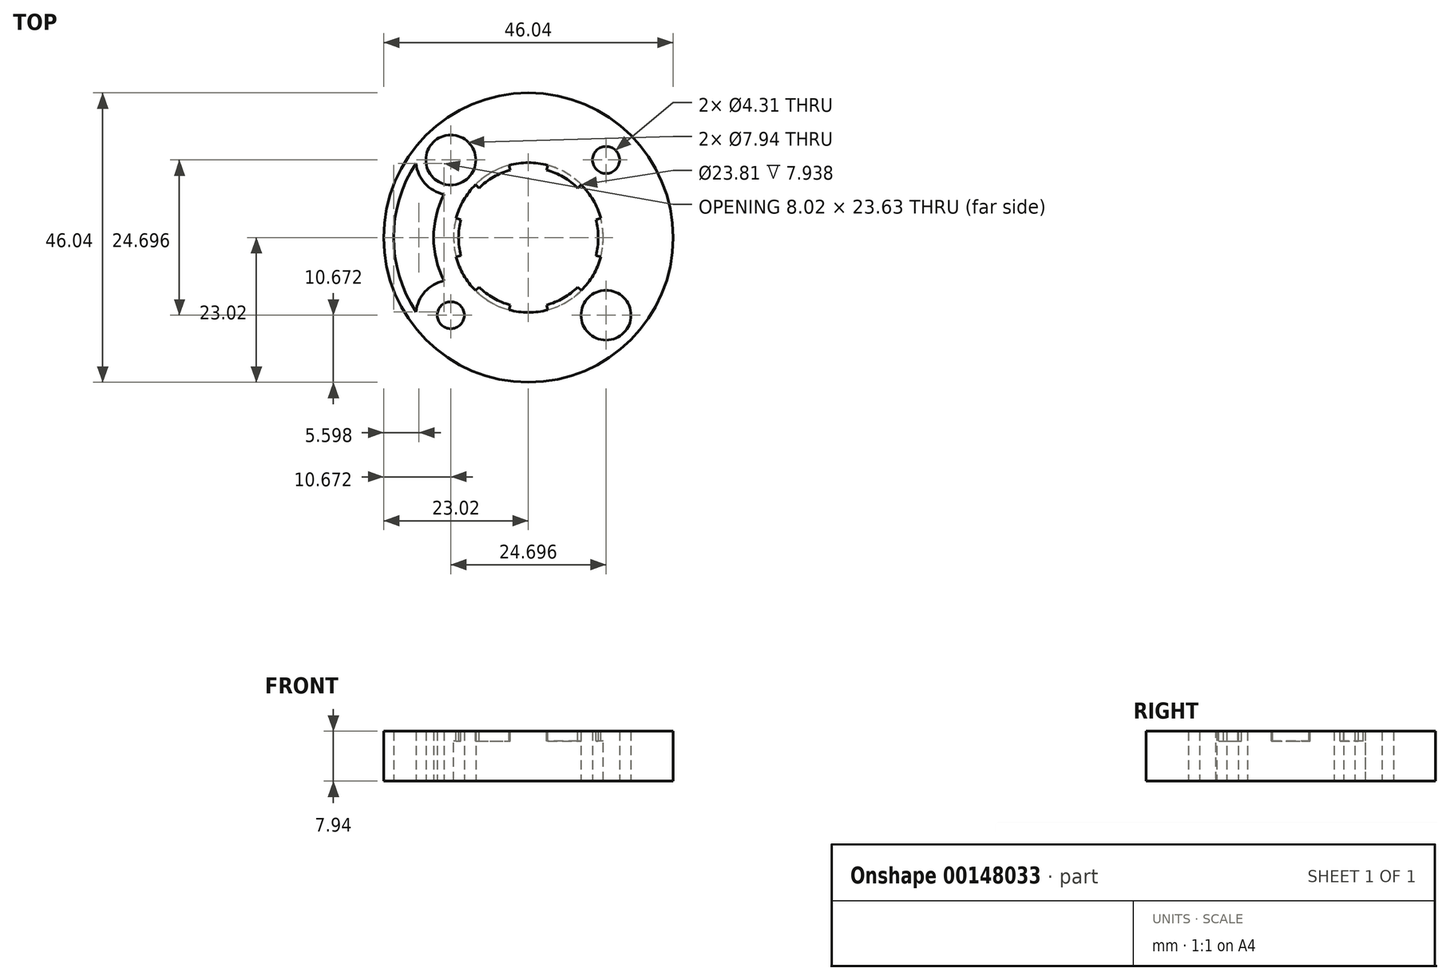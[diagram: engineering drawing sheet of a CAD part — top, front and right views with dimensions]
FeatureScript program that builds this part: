
annotation { "Feature Type Name" : "Feature", "Feature Type Description" : "" }
export const myFeature = defineFeature(function(context is Context, id is Id, definition is map)
    precondition{}
    {
        {
            var Q0;
            Q0=qCreatedBy(makeId("Top.planeOp"),FACE);
            var sketch = newSketch(context, id + "F0", { "sketchPlane" : qUnion([Q0])});
            skCircle(sketch, "E0", {"center": v(0, 0) * mm, "radius": 23.02 * mm});
            skCircle(sketch, "E1", {"center": v(0, 0) * mm, "radius": 11.9 * mm, "construction": true});
            skLineSegment(sketch, "E2.bottom", {"start": v(-12.35, 12.35) * mm, "end": v(12.35, 12.35) * mm, "construction": true});
            skLineSegment(sketch, "E2.top", {"start": v(-12.35, -12.35) * mm, "end": v(12.35, -12.35) * mm, "construction": true});
            skLineSegment(sketch, "E2.left", {"start": v(-12.35, 12.35) * mm, "end": v(-12.35, -12.35) * mm, "construction": true});
            skLineSegment(sketch, "E2.right", {"start": v(12.35, 12.35) * mm, "end": v(12.35, -12.35) * mm, "construction": true});
            skCircle(sketch, "E3", {"center": v(-12.35, 12.35) * mm, "radius": 5.56 * mm, "construction": true});
            skCircle(sketch, "E4", {"center": v(12.35, 12.35) * mm, "radius": 2.15 * mm});
            skCircle(sketch, "E5", {"center": v(-12.35, 12.35) * mm, "radius": 3.97 * mm});
            skCircle(sketch, "E6", {"center": v(-12.35, -12.35) * mm, "radius": 2.15 * mm});
            skCircle(sketch, "E7", {"center": v(12.35, -12.35) * mm, "radius": 3.97 * mm});
            skCircle(sketch, "E8", {"center": v(0, 0) * mm, "radius": 11.11 * mm});
            skSolve(sketch);
        }
        {
            var Q0;
            Q0=qSketchRegion(id+"F0",true);
            extrude(context, id + "F1", {"entities" : qUnion([Q0]), "depth" : 7.94 * mm});
        }
        {
            var Q0;
            Q0=makeQuery(id+"F1.opExtrude","CAP_FACE",FACE,{"disambiguationData":[OSD([sQuery(id+"F0.wireOp",EDGE,"E0"),sQuery(id+"F0.wireOp",EDGE,"E1"),sQuery(id+"F0.wireOp",EDGE,"E4"),sQuery(id+"F0.wireOp",EDGE,"E5"),sQuery(id+"F0.wireOp",EDGE,"E6"),sQuery(id+"F0.wireOp",EDGE,"E7")])],"isStart":false});
            var sketch = newSketch(context, id + "F2", { "sketchPlane" : qUnion([Q0])});
            skLineSegment(sketch, "E9", {"start": v(0, 0) * mm, "end": v(0, 11.11) * mm, "construction": true});
            skLineSegment(sketch, "E10", {"start": v(0, 0) * mm, "end": v(-2.88, 10.73) * mm, "construction": true});
            skLineSegment(sketch, "E11", {"start": v(0, 0) * mm, "end": v(2.88, 10.73) * mm, "construction": true});
            skLineSegment(sketch, "E12", {"start": v(-2.88, 10.73) * mm, "end": v(-3.08, 11.5) * mm});
            skLineSegment(sketch, "E13", {"start": v(2.88, 10.73) * mm, "end": v(3.08, 11.5) * mm});
            skArc(sketch, "E14", {"start": v(2.88, 10.73) * mm, "mid": v(0, 11.11) * mm, "end": v(-2.88, 10.73) * mm});
            skArc(sketch, "E15", {"start": v(3.08, 11.5) * mm, "mid": v(0, 11.9) * mm, "end": v(-3.08, 11.5) * mm});
            skSolve(sketch);
        }
        {
            var Q0;
            Q0=qSketchRegion(id+"F2",true);
            var Q1;
            Q1=makeQuery(id+"F1.opExtrude","CAP_FACE",FACE,{"disambiguationData":[OSD([sQuery(id+"F0.wireOp",EDGE,"E0"),sQuery(id+"F0.wireOp",EDGE,"E4"),sQuery(id+"F0.wireOp",EDGE,"E5"),sQuery(id+"F0.wireOp",EDGE,"E6"),sQuery(id+"F0.wireOp",EDGE,"E7"),sQuery(id+"F0.wireOp",EDGE,"E8")])],"isStart":true});
            extrude(context, id + "F3", {"entities" : qUnion([Q0]), "operationType" : NewBodyOperationType.REMOVE, "endBound" : BoundingType.UP_TO_SURFACE, "oppositeDirection" : true, "endBoundEntityFace" : qUnion([Q1]), "depth" : 25.4 * mm});
        }
        {
            var Q0;
            Q0=makeQuery(id+"F3.boolean.opBoolean","COPY",FACE,{"derivedFrom":makeQuery(id+"F3.opExtrude","SWEPT_FACE",FACE,{"disambiguationData":[OSD([sQuery(id+"F2.wireOp",EDGE,"E12")])]})});
            var Q1;
            Q1=makeQuery(id+"F3.boolean.opBoolean","COPY",FACE,{"derivedFrom":makeQuery(id+"F3.opExtrude","SWEPT_FACE",FACE,{"disambiguationData":[OSD([sQuery(id+"F2.wireOp",EDGE,"E15")])]})});
            var Q2;
            Q2=makeQuery(id+"F3.boolean.opBoolean","COPY",FACE,{"derivedFrom":makeQuery(id+"F3.opExtrude","SWEPT_FACE",FACE,{"disambiguationData":[OSD([sQuery(id+"F2.wireOp",EDGE,"E13")])]})});
            var Q3;
            Q3=makeQuery(id+"F1.opExtrude","SWEPT_FACE",FACE,{"disambiguationData":[OSD([sQuery(id+"F0.wireOp",EDGE,"E8")])]});
            circularPattern(context, id + "F4", {"patternType" : PatternType.FACE, "faces" : qUnion([Q0, Q1, Q2]), "axis" : qUnion([Q3]), "angle" : 60 * degree, "instanceCount" : 6});
        }
        {
            var Q0;
            Q0=makeQuery(id+"F1.opExtrude","CAP_FACE",FACE,{"disambiguationData":[OSD([sQuery(id+"F0.wireOp",EDGE,"E0"),sQuery(id+"F0.wireOp",EDGE,"E4"),sQuery(id+"F0.wireOp",EDGE,"E5"),sQuery(id+"F0.wireOp",EDGE,"E6"),sQuery(id+"F0.wireOp",EDGE,"E7"),sQuery(id+"F0.wireOp",EDGE,"E8")])],"isStart":false});
            cPlane(context, id + "F5", {"entities" : qUnion([Q0]), "cplaneType" : CPlaneType.OFFSET, "offset" : 1.59 * mm, "oppositeDirection" : true, "width" : 152.4 * mm, "height" : 152.4 * mm});
        }
        {
            var Q0;
            Q0=makeQuery(id+"F1.opExtrude","CAP_FACE",FACE,{"disambiguationData":[OSD([sQuery(id+"F0.wireOp",EDGE,"E0"),sQuery(id+"F0.wireOp",EDGE,"E4"),sQuery(id+"F0.wireOp",EDGE,"E5"),sQuery(id+"F0.wireOp",EDGE,"E6"),sQuery(id+"F0.wireOp",EDGE,"E7"),sQuery(id+"F0.wireOp",EDGE,"E8")])],"isStart":true});
            var sketch = newSketch(context, id + "F6", { "sketchPlane" : qUnion([Q0])});
            skCircle(sketch, "E16", {"center": v(0, 0) * mm, "radius": 11.9 * mm});
            skSolve(sketch);
        }
        {
            var Q0;
            Q0=qSketchRegion(id+"F6",true);
            var Q1;
            Q1=qCreatedBy(id+"F5.planeOp",FACE);
            extrude(context, id + "F7", {"entities" : qUnion([Q0]), "operationType" : NewBodyOperationType.REMOVE, "endBound" : BoundingType.UP_TO_SURFACE, "oppositeDirection" : true, "endBoundEntityFace" : qUnion([Q1]), "depth" : 25.4 * mm});
        }
        {
            var Q0;
            Q0=makeQuery(id+"F1.opExtrude","CAP_FACE",FACE,{"disambiguationData":[OSD([sQuery(id+"F0.wireOp",EDGE,"E0"),sQuery(id+"F0.wireOp",EDGE,"E4"),sQuery(id+"F0.wireOp",EDGE,"E5"),sQuery(id+"F0.wireOp",EDGE,"E6"),sQuery(id+"F0.wireOp",EDGE,"E7"),sQuery(id+"F0.wireOp",EDGE,"E8")])],"isStart":true});
            var sketch = newSketch(context, id + "F8", { "sketchPlane" : qUnion([Q0])});
            skArc(sketch, "E17", {"start": v(-17.88, 11.82) * mm, "mid": v(-16.46, 8.61) * mm, "end": v(-13.41, 6.9) * mm});
            skArc(sketch, "E18", {"start": v(-13.41, -6.9) * mm, "mid": v(-16.46, -8.61) * mm, "end": v(-17.88, -11.82) * mm});
            skArc(sketch, "E19", {"start": v(-13.41, 6.9) * mm, "mid": v(-15.08, 0) * mm, "end": v(-13.41, -6.9) * mm});
            skArc(sketch, "E20", {"start": v(-17.88, 11.82) * mm, "mid": v(-21.43, 0) * mm, "end": v(-17.88, -11.82) * mm});
            skSolve(sketch);
        }
        {
            var Q0;
            Q0=qSketchRegion(id+"F8",true);
            var Q1;
            Q1=makeQuery(id+"F1.opExtrude","CAP_FACE",FACE,{"disambiguationData":[OSD([sQuery(id+"F0.wireOp",EDGE,"E0"),sQuery(id+"F0.wireOp",EDGE,"E4"),sQuery(id+"F0.wireOp",EDGE,"E5"),sQuery(id+"F0.wireOp",EDGE,"E6"),sQuery(id+"F0.wireOp",EDGE,"E7"),sQuery(id+"F0.wireOp",EDGE,"E8")])],"isStart":false});
            extrude(context, id + "F9", {"entities" : qUnion([Q0]), "operationType" : NewBodyOperationType.REMOVE, "endBound" : BoundingType.UP_TO_SURFACE, "oppositeDirection" : true, "endBoundEntityFace" : qUnion([Q1]), "depth" : 25.4 * mm});
        }
    });
